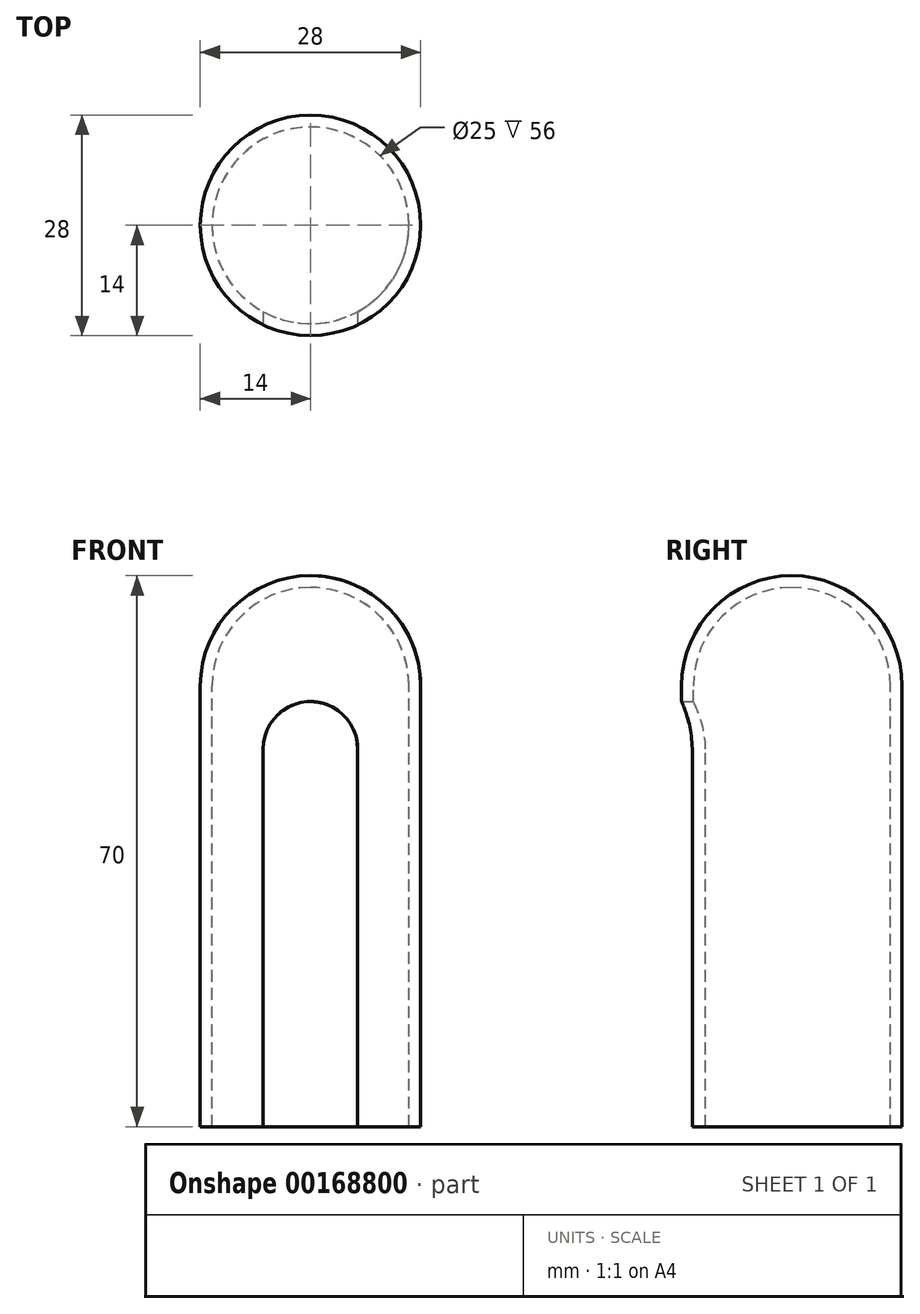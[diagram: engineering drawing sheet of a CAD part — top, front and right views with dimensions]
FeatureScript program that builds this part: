
annotation { "Feature Type Name" : "Feature", "Feature Type Description" : "" }
export const myFeature = defineFeature(function(context is Context, id is Id, definition is map)
    precondition{}
    {
        {
            var Q0;
            Q0=qCreatedBy(makeId("Front.planeOp"),FACE);
            var sketch = newSketch(context, id + "F0", { "sketchPlane" : qUnion([Q0])});
            skArc(sketch, "E0", {"start": v(0, 68.5) * mm, "mid": v(-8.84, 64.84) * mm, "end": v(-12.5, 56) * mm});
            skArc(sketch, "E1", {"start": v(0, 70) * mm, "mid": v(-9.9, 65.9) * mm, "end": v(-14, 56) * mm});
            skLineSegment(sketch, "E2", {"start": v(-12.5, 56) * mm, "end": v(-14, 56) * mm});
            skLineSegment(sketch, "E3", {"start": v(12.5, 56) * mm, "end": v(14, 56) * mm});
            skLineSegment(sketch, "E4", {"start": v(-12.5, 56) * mm, "end": v(0, 56) * mm, "construction": true});
            skLineSegment(sketch, "E5", {"start": v(0, 56) * mm, "end": v(12.5, 56) * mm, "construction": true});
            skLineSegment(sketch, "E6", {"start": v(-14, 56) * mm, "end": v(-14, 0) * mm});
            skLineSegment(sketch, "E7", {"start": v(-14, 0) * mm, "end": v(-12.5, 0) * mm});
            skLineSegment(sketch, "E8", {"start": v(-12.5, 56) * mm, "end": v(-12.5, 0) * mm});
            skLineSegment(sketch, "E9", {"start": v(0, 68.5) * mm, "end": v(0, 70) * mm});
            skPoint(sketch, "E10.orphan", {"position": v(0, 0) * mm});
            skLineSegment(sketch, "E11", {"start": v(0, 56) * mm, "end": v(0, 0) * mm, "construction": true});
            skSolve(sketch);
        }
        {
            var Q0;
            Q0 = qSketchRegion(id + "F0", true);
            var Q1;
            Q1=sQuery(id+"F0.wireOp",EDGE,"E11");
            revolve(context, id + "F1", {"entities" : qUnion([Q0]), "axis" : qUnion([Q1]), "revolveType" : RevolveType.FULL});
        }
        {
            var Q0;
            Q0=qCreatedBy(makeId("Front.planeOp"),FACE);
            var sketch = newSketch(context, id + "F2", { "sketchPlane" : qUnion([Q0])});
            skArc(sketch, "E12", {"start": v(6, 48) * mm, "mid": v(0, 54) * mm, "end": v(-6, 48) * mm});
            skLineSegment(sketch, "E13", {"start": v(0, 48) * mm, "end": v(-6, 48) * mm, "construction": true});
            skLineSegment(sketch, "E14", {"start": v(-6, 48) * mm, "end": v(-6, -2.99) * mm});
            skLineSegment(sketch, "E15", {"start": v(-6, -2.99) * mm, "end": v(6, -2.99) * mm});
            skLineSegment(sketch, "E16", {"start": v(0, 48) * mm, "end": v(6, 48) * mm, "construction": true});
            skLineSegment(sketch, "E17", {"start": v(6, 48) * mm, "end": v(6, -2.99) * mm});
            skLineSegment(sketch, "E18", {"start": v(0, 70) * mm, "end": v(-35.6, 70) * mm, "construction": true});
            skLineSegment(sketch, "E19", {"start": v(0, 54) * mm, "end": v(-31.54, 54) * mm, "construction": true});
            skSolve(sketch);
        }
        {
            var Q0;
            Q0 = qSketchRegion(id + "F2", true);
            var Q1;
            Q1 = qConstructionFilter(qBodyType(qCreatedBy(id + "F2" ,EDGE), BodyType.WIRE), ConstructionObject.NO);
            extrude(context, id + "F3", {"entities" : qUnion([Q0]), "operationType" : NewBodyOperationType.REMOVE, "surfaceEntities" : qUnion([Q1]), "depth" : 25 * mm});
        }
    });
